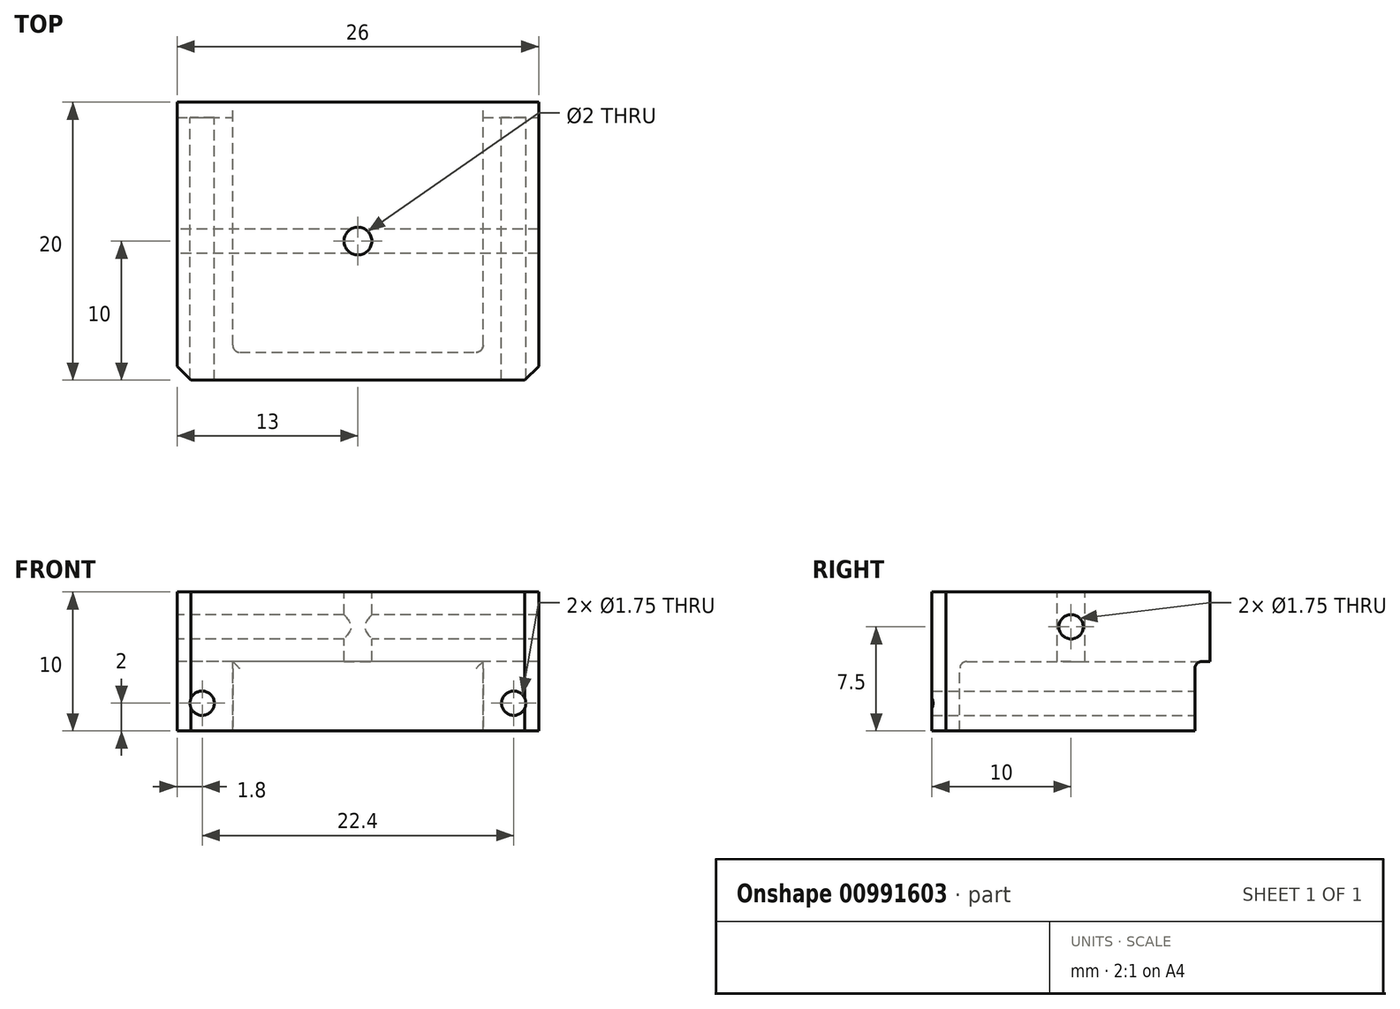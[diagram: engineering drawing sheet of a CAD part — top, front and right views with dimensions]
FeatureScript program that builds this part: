
annotation { "Feature Type Name" : "Feature", "Feature Type Description" : "" }
export const myFeature = defineFeature(function(context is Context, id is Id, definition is map)
    precondition{}
    {
        {
            var Q0;
            Q0=qCreatedBy(makeId("Top.planeOp"),FACE);
            var sketch = newSketch(context, id + "F0", { "sketchPlane" : qUnion([Q0])});
            skLineSegment(sketch, "E0.bottom", {"start": v(-13, 10) * mm, "end": v(13, 10) * mm});
            skLineSegment(sketch, "E0.top", {"start": v(-13, -10) * mm, "end": v(13, -10) * mm});
            skLineSegment(sketch, "E0.left", {"start": v(-13, 10) * mm, "end": v(-13, -10) * mm});
            skLineSegment(sketch, "E0.right", {"start": v(13, 10) * mm, "end": v(13, -10) * mm});
            skLineSegment(sketch, "E1", {"start": v(0, 65.84) * mm, "end": v(0, -65.84) * mm, "construction": true});
            skLineSegment(sketch, "E2", {"start": v(-87.05, 0) * mm, "end": v(87.05, 0) * mm, "construction": true});
            skSolve(sketch);
        }
        {
            var Q0;
            Q0=qSketchRegion(id+"F0",true);
            extrude(context, id + "F1", {"entities" : qUnion([Q0]), "depth" : 10 * mm, "offsetDistance" : 25 * mm});
        }
        {
            var Q0;
            Q0=makeQuery(id+"F1.opExtrude","SWEPT_FACE",FACE,{"disambiguationData":[OSD([sQuery(id+"F0.wireOp",EDGE,"E0.bottom")])]});
            var sketch = newSketch(context, id + "F2", { "sketchPlane" : qUnion([Q0])});
            skLineSegment(sketch, "E3.bottom", {"start": v(-9, 0) * mm, "end": v(9, 0) * mm});
            skLineSegment(sketch, "E3.top", {"start": v(-9, 5) * mm, "end": v(9, 5) * mm});
            skLineSegment(sketch, "E3.left", {"start": v(-9, 0) * mm, "end": v(-9, 5) * mm});
            skLineSegment(sketch, "E3.right", {"start": v(9, 0) * mm, "end": v(9, 5) * mm});
            skLineSegment(sketch, "E4", {"start": v(0, -0.33) * mm, "end": v(0, 10.8) * mm, "construction": true});
            skSolve(sketch);
        }
        {
            var Q0;
            Q0=qSketchRegion(id+"F2",true);
            extrude(context, id + "F3", {"entities" : qUnion([Q0]), "operationType" : NewBodyOperationType.REMOVE, "oppositeDirection" : true, "depth" : 18 * mm, "offsetDistance" : 25 * mm});
        }
        {
            var Q0;
            Q0=makeQuery(id+"F1.opExtrude","SWEPT_FACE",FACE,{"disambiguationData":[OSD([sQuery(id+"F0.wireOp",EDGE,"E0.bottom")])]});
            var sketch = newSketch(context, id + "F4", { "sketchPlane" : qUnion([Q0])});
            skLineSegment(sketch, "E5.bottom", {"start": v(-13, 0) * mm, "end": v(13, 0) * mm});
            skLineSegment(sketch, "E5.top", {"start": v(-13, 5) * mm, "end": v(13, 5) * mm});
            skLineSegment(sketch, "E5.left", {"start": v(-13, 0) * mm, "end": v(-13, 5) * mm});
            skLineSegment(sketch, "E5.right", {"start": v(13, 0) * mm, "end": v(13, 5) * mm});
            skSolve(sketch);
        }
        {
            var Q0;
            Q0=qSketchRegion(id+"F4",true);
            extrude(context, id + "F5", {"entities" : qUnion([Q0]), "operationType" : NewBodyOperationType.REMOVE, "oppositeDirection" : true, "depth" : 1.1 * mm, "offsetDistance" : 25 * mm});
        }
        {
            var Q0;
            Q0=makeQuery(id+"F3.boolean.opBoolean","COPY",EDGE,{"derivedFrom":makeQuery(id+"F3.opExtrude","CAP_EDGE",EDGE,{"disambiguationData":[OSD([sQuery(id+"F2.wireOp",EDGE,"E3.left")])],"isStart":false})});
            var Q1;
            Q1=makeQuery(id+"F3.boolean.opBoolean","COPY",EDGE,{"derivedFrom":makeQuery(id+"F3.opExtrude","CAP_EDGE",EDGE,{"disambiguationData":[OSD([sQuery(id+"F2.wireOp",EDGE,"E3.right")])],"isStart":false})});
            var Q2;
            Q2=makeQuery(id+"F3.boolean.opBoolean","COPY",EDGE,{"derivedFrom":makeQuery(id+"F3.opExtrude","CAP_EDGE",EDGE,{"disambiguationData":[OSD([sQuery(id+"F2.wireOp",EDGE,"E3.top")])],"isStart":false})});
            fillet(context, id + "F6", {"entities" : qUnion([Q0, Q1, Q2]), "radius" : 0.5 * mm, "tangentPropagation" : true, "allowEdgeOverflow" : false});
        }
        {
            var Q0;
            {var subQ0=sQuery(id+"F4.wireOp",EDGE,"E5.top");Q0=makeQuery(id+"F5.boolean.opBoolean","COPY",EDGE,{"disambiguationData":[TD([makeQuery(id+"F1.opExtrude","SWEPT_FACE",FACE,{"disambiguationData":[OSD([sQuery(id+"F0.wireOp",EDGE,"E0.left")])]})])],"derivedFrom":makeQuery(id+"F5.opExtrude","CAP_EDGE",EDGE,{"disambiguationData":[OSD([subQ0])],"isStart":false})});}
            var Q1;
            {var subQ0=sQuery(id+"F4.wireOp",EDGE,"E5.top");Q1=makeQuery(id+"F5.boolean.opBoolean","COPY",EDGE,{"disambiguationData":[TD([makeQuery(id+"F1.opExtrude","SWEPT_FACE",FACE,{"disambiguationData":[OSD([sQuery(id+"F0.wireOp",EDGE,"E0.right")])]})])],"derivedFrom":makeQuery(id+"F5.opExtrude","CAP_EDGE",EDGE,{"disambiguationData":[OSD([subQ0])],"isStart":false})});}
            fillet(context, id + "F7", {"entities" : qUnion([Q0, Q1]), "radius" : 0.5 * mm, "tangentPropagation" : true, "allowEdgeOverflow" : false});
        }
        {
            var Q0;
            Q0=makeQuery(id+"F1.opExtrude","SWEPT_EDGE",EDGE,{"disambiguationData":[OSD([sQuery(id+"F0.wireOp",EDGE,"E0.top"),sQuery(id+"F0.wireOp",EDGE,"E0.right")])]});
            var Q1;
            Q1=makeQuery(id+"F1.opExtrude","SWEPT_EDGE",EDGE,{"disambiguationData":[OSD([sQuery(id+"F0.wireOp",EDGE,"E0.top"),sQuery(id+"F0.wireOp",EDGE,"E0.left")])]});
            chamfer(context, id + "F8", {"entities" : qUnion([Q0, Q1]), "width" : 1 * mm, "tangentPropagation" : true});
        }
        {
            var Q0;
            {var subQ0=sQuery(id+"F0.wireOp",EDGE,"E0.left");var subQ1=sQuery(id+"F4.wireOp",EDGE,"E5.top");Q0=makeQuery(id+"F5.boolean.opBoolean","COPY",FACE,{"disambiguationData":[TD([makeQuery(id+"F1.opExtrude","SWEPT_FACE",FACE,{"disambiguationData":[OSD([subQ0])]})])],"derivedFrom":makeQuery(id+"F5.opExtrude","CAP_FACE",FACE,{"disambiguationData":[OSD([sQuery(id+"F4.wireOp",EDGE,"E5.bottom"),subQ1,sQuery(id+"F4.wireOp",EDGE,"E5.left"),sQuery(id+"F4.wireOp",EDGE,"E5.right")])],"isStart":false})});}
            var sketch = newSketch(context, id + "F9", { "sketchPlane" : qUnion([Q0])});
            skPoint(sketch, "E6", {"position": v(-11.2, 2) * mm});
            skPoint(sketch, "E7", {"position": v(11.2, 2) * mm});
            skSolve(sketch);
        }
        {
            var Q0;
            Q0=sQuery(id+"F9.wireOp",VERTEX,"E6");
            var Q1;
            Q1=sQuery(id+"F9.wireOp",VERTEX,"E7");
            var Q2;
            Q2=makeQuery(id+"F1.opExtrude","SWEPT_BODY",BODY,{"disambiguationData":[OSD([sQuery(id+"F0.wireOp",EDGE,"E0.bottom"),sQuery(id+"F0.wireOp",EDGE,"E0.top"),sQuery(id+"F0.wireOp",EDGE,"E0.left"),sQuery(id+"F0.wireOp",EDGE,"E0.right"),sQuery(id+"F0.wireOp",EDGE,"H4gdiPJo-8vIM-zMkF-eMMu-KdfANKpb1p3E")])]});
            hole(context, id + "F10", {"style" : HoleStyle.SIMPLE, "endStyle" : HoleEndStyle.THROUGH, "standardTappedOrClearance" : lookupTablePath({ "standard" : "ISO", "engagement" : "75%", "pitch" : "0.25 mm", "size" : "M2", "type" : "Tapped" }), "standardBlindInLast" : lookupTablePath({ "standard" : "ISO", "fit" : "Normal", "engagement" : "75%", "pitch" : "0.25 mm", "size" : "M2", "type" : "Clearance & tapped" }), "holeDiameter" : 1.75 * mm, "majorDiameter" : 2 * mm, "showTappedDepth" : true, "isTappedThrough" : true, "tappedDepth" : 12 * mm, "tapClearance" : 3, "locations" : qUnion([Q0, Q1]), "scope" : qUnion([Q2])});
        }
        {
            var Q0;
            Q0=makeQuery(id+"F1.opExtrude","SWEPT_FACE",FACE,{"disambiguationData":[OSD([sQuery(id+"F0.wireOp",EDGE,"E0.left")])]});
            var sketch = newSketch(context, id + "F11", { "sketchPlane" : qUnion([Q0])});
            skPoint(sketch, "E8", {"position": v(0, 7.5) * mm});
            skSolve(sketch);
        }
        {
            var Q0;
            Q0=sQuery(id+"F11.wireOp",VERTEX,"E8");
            var Q1;
            Q1=makeQuery(id+"F1.opExtrude","SWEPT_BODY",BODY,{"disambiguationData":[OSD([sQuery(id+"F0.wireOp",EDGE,"E0.bottom"),sQuery(id+"F0.wireOp",EDGE,"E0.top"),sQuery(id+"F0.wireOp",EDGE,"E0.left"),sQuery(id+"F0.wireOp",EDGE,"E0.right"),sQuery(id+"F0.wireOp",EDGE,"H4gdiPJo-8vIM-zMkF-eMMu-KdfANKpb1p3E")])]});
            hole(context, id + "F12", {"style" : HoleStyle.SIMPLE, "endStyle" : HoleEndStyle.THROUGH, "standardTappedOrClearance" : lookupTablePath({ "standard" : "ISO", "engagement" : "75%", "pitch" : "0.25 mm", "size" : "M2", "type" : "Tapped" }), "standardBlindInLast" : lookupTablePath({ "standard" : "ISO", "fit" : "Normal", "engagement" : "75%", "pitch" : "0.25 mm", "size" : "M2", "type" : "Clearance & tapped" }), "holeDiameter" : 1.75 * mm, "majorDiameter" : 2 * mm, "showTappedDepth" : true, "isTappedThrough" : true, "tappedDepth" : 12 * mm, "tapClearance" : 3, "locations" : qUnion([Q0]), "scope" : qUnion([Q1])});
        }
        {
            var Q0;
            Q0=makeQuery(id+"F1.opExtrude","CAP_FACE",FACE,{"disambiguationData":[OSD([sQuery(id+"F0.wireOp",EDGE,"E0.bottom"),sQuery(id+"F0.wireOp",EDGE,"E0.top"),sQuery(id+"F0.wireOp",EDGE,"E0.left"),sQuery(id+"F0.wireOp",EDGE,"E0.right")])],"isStart":false});
            var sketch = newSketch(context, id + "F13", { "sketchPlane" : qUnion([Q0])});
            skPoint(sketch, "E9", {"position": v(0, 0) * mm});
            skLineSegment(sketch, "E10", {"start": v(0, 4.4) * mm, "end": v(0, -3.34) * mm, "construction": true});
            skLineSegment(sketch, "E11", {"start": v(-6.6, 0) * mm, "end": v(8.03, 0) * mm, "construction": true});
            skSolve(sketch);
        }
        {
            var Q0;
            Q0=sQuery(id+"F13.wireOp",VERTEX,"E9");
            var Q1;
            Q1=makeQuery(id+"F1.opExtrude","SWEPT_BODY",BODY,{"disambiguationData":[OSD([sQuery(id+"F0.wireOp",EDGE,"E0.bottom"),sQuery(id+"F0.wireOp",EDGE,"E0.top"),sQuery(id+"F0.wireOp",EDGE,"E0.left"),sQuery(id+"F0.wireOp",EDGE,"E0.right")])]});
            hole(context, id + "F14", {"style" : HoleStyle.SIMPLE, "endStyle" : HoleEndStyle.THROUGH, "holeDiameter" : 2 * mm, "majorDiameter" : 2 * mm, "isTappedThrough" : true, "tappedDepth" : 12 * mm, "tapClearance" : 3, "locations" : qUnion([Q0]), "scope" : qUnion([Q1])});
        }
    });
